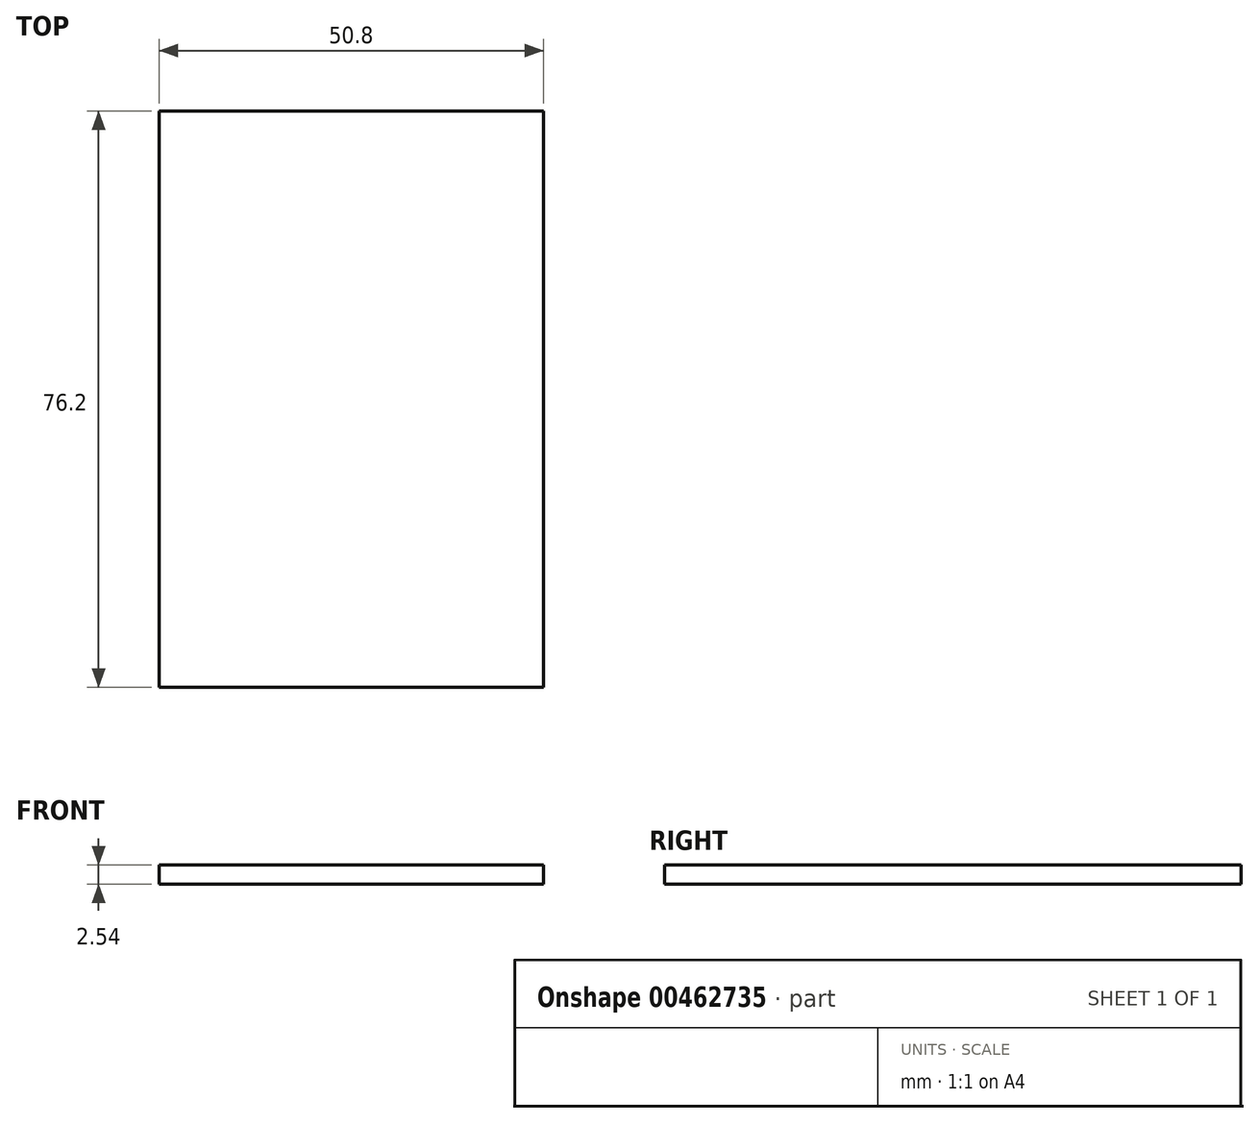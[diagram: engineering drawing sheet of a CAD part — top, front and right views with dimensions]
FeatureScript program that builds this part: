
annotation { "Feature Type Name" : "Feature", "Feature Type Description" : "" }
export const myFeature = defineFeature(function(context is Context, id is Id, definition is map)
    precondition{}
    {
        {
            var Q0;
            Q0=qCreatedBy(makeId("Top.planeOp"),FACE);
            var sketch = newSketch(context, id + "F0", { "sketchPlane" : qUnion([Q0])});
            skLineSegment(sketch, "E0.bottom", {"start": v(-45.1, 54.53) * mm, "end": v(5.7, 54.53) * mm});
            skLineSegment(sketch, "E0.top", {"start": v(-45.1, -21.67) * mm, "end": v(5.7, -21.67) * mm});
            skLineSegment(sketch, "E0.left", {"start": v(-45.1, 54.53) * mm, "end": v(-45.1, -21.67) * mm});
            skLineSegment(sketch, "E0.right", {"start": v(5.7, 54.53) * mm, "end": v(5.7, -21.67) * mm});
            skSolve(sketch);
        }
        {
            var Q0;
            Q0=makeQuery(id+"F0.imprint","IMPRINT",FACE,{"disambiguationData":[TD([[makeQuery(id+"F0.imprint","IMPRINT",EDGE,{"derivedFrom":sQuery(id+"F0.wireOp",EDGE,"E0.bottom")}),-1.0]])]});
            var Q1;
            Q1 = qSketchRegion(id + "F0", true);
            extrude(context, id + "F1", {"entities" : qUnion([Q0, Q1]), "depth" : 2.54 * mm});
        }
    });
